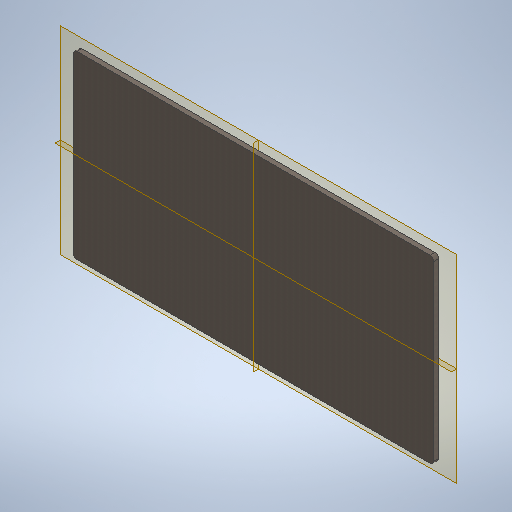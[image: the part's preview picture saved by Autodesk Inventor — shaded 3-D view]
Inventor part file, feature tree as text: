
AUTODESK INVENTOR PART (.ipt)
format: ipt  version: 2025.2 (Build 292293000, 293)  size: 264,192 bytes
history: native  units: mm
features: fillet x4, extrude x1, sketch x1
ambient origin geometry x8: Origin, YZ Plane, XZ Plane, XY Plane, X Axis, Y Axis, Z Axis, Center Point
bodies: Solid1 (feature_tree)
feature tree (6):
  extrude  "Extrusion1"  Depth=750.0mm
  fillet  "Fillet1"  Radius=20.0mm
  fillet  "Fillet2"  Radius=15.0mm
  fillet  "Fillet3"  Radius=15.0mm
  fillet  "Fillet4"  Radius=15.0mm
  sketch  "Sketch2"  dims[d0=1500.0mm d1=750.0mm d2=20.0mm d3=0.0mm d4=15.0mm d5=15.0mm d6=15.0mm d7=15.0mm]
